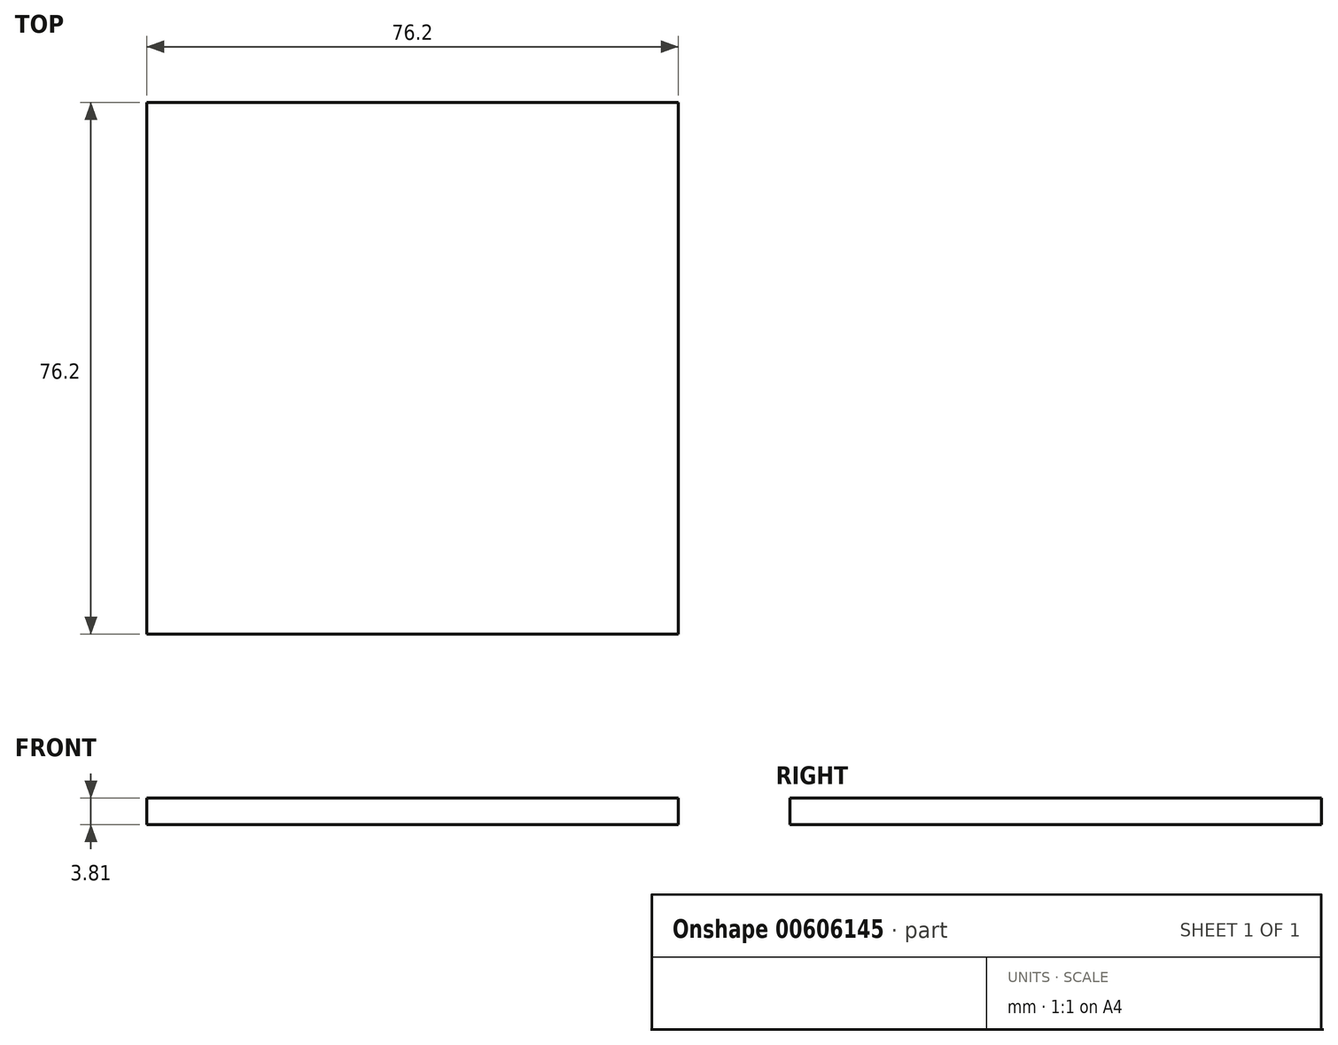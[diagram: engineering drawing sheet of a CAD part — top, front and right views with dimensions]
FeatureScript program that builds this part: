
annotation { "Feature Type Name" : "Feature", "Feature Type Description" : "" }
export const myFeature = defineFeature(function(context is Context, id is Id, definition is map)
    precondition{}
    {
        {
            var Q0;
            Q0=qCreatedBy(makeId("Top.planeOp"),FACE);
            var sketch = newSketch(context, id + "F0", { "sketchPlane" : qUnion([Q0])});
            skLineSegment(sketch, "E0.bottom", {"start": v(-40.77, 43.58) * mm, "end": v(35.43, 43.58) * mm});
            skLineSegment(sketch, "E0.top", {"start": v(-40.77, -32.62) * mm, "end": v(35.43, -32.62) * mm});
            skLineSegment(sketch, "E0.left", {"start": v(-40.77, 43.58) * mm, "end": v(-40.77, -32.62) * mm});
            skLineSegment(sketch, "E0.right", {"start": v(35.43, 43.58) * mm, "end": v(35.43, -32.62) * mm});
            skSolve(sketch);
        }
        {
            var Q0;
            Q0=makeQuery(id+"F0.imprint","IMPRINT",FACE,{"disambiguationData":[TD([[makeQuery(id+"F0.imprint","IMPRINT",EDGE,{"derivedFrom":sQuery(id+"F0.wireOp",EDGE,"E0.bottom")}),-1.0]])]});
            extrude(context, id + "F1", {"entities" : qUnion([Q0]), "depth" : 3.8 * mm, "offsetDistance" : 25.4 * mm});
        }
    });
